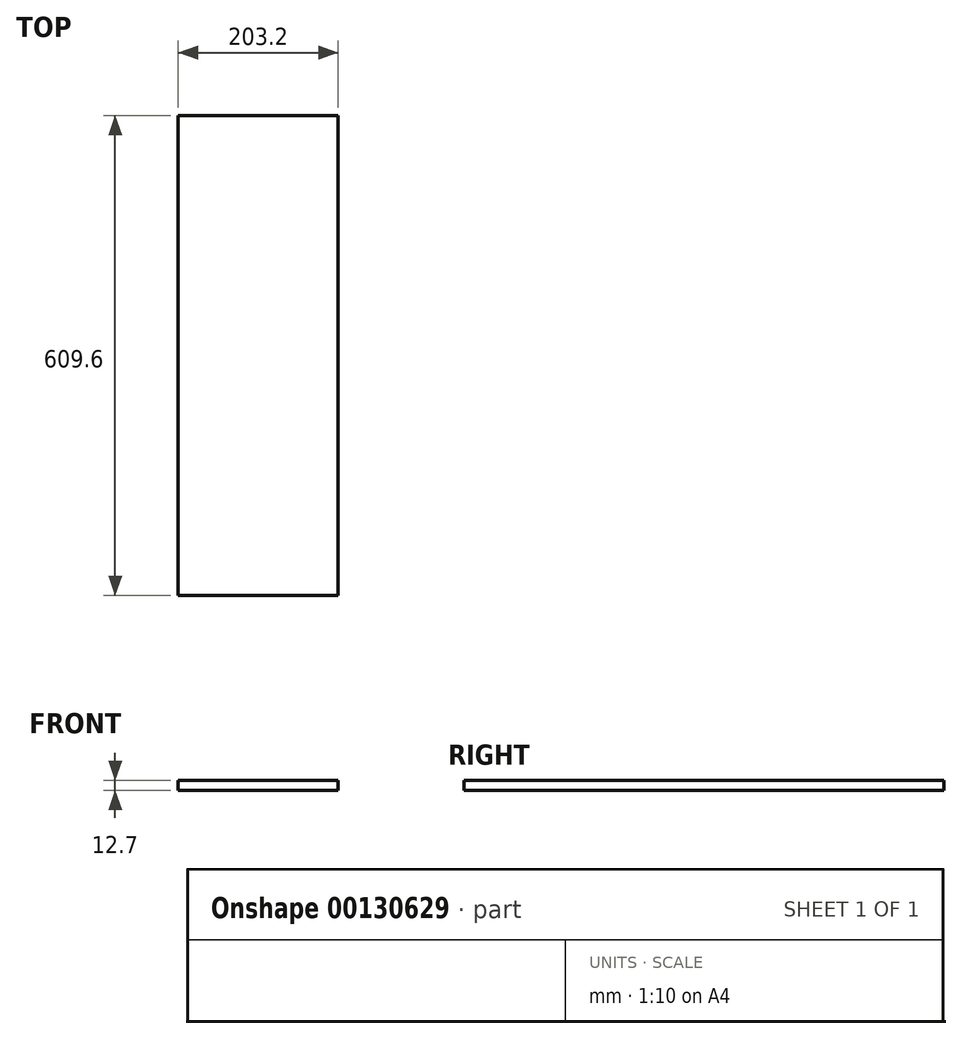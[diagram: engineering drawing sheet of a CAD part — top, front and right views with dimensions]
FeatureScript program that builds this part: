
annotation { "Feature Type Name" : "Feature", "Feature Type Description" : "" }
export const myFeature = defineFeature(function(context is Context, id is Id, definition is map)
    precondition{}
    {
        {
            var Q0;
            Q0=qCreatedBy(makeId("Top.planeOp"),FACE);
            var sketch = newSketch(context, id + "F0", { "sketchPlane" : qUnion([Q0])});
            skLineSegment(sketch, "E0.bottom", {"start": v(0, 0) * mm, "end": v(203.2, 0) * mm});
            skLineSegment(sketch, "E0.top", {"start": v(0, 609.6) * mm, "end": v(203.2, 609.6) * mm});
            skLineSegment(sketch, "E0.left", {"start": v(0, 0) * mm, "end": v(0, 609.6) * mm});
            skLineSegment(sketch, "E0.right", {"start": v(203.2, 0) * mm, "end": v(203.2, 609.6) * mm});
            skSolve(sketch);
        }
        {
            var Q0;
            Q0=makeQuery(id+"F0.imprint","IMPRINT",FACE,{"disambiguationData":[TD([[makeQuery(id+"F0.imprint","IMPRINT",EDGE,{"derivedFrom":sQuery(id+"F0.wireOp",EDGE,"E0.bottom")}),1.0]])]});
            extrude(context, id + "F1", {"entities" : qUnion([Q0]), "depth" : 12.7 * mm});
        }
    });
